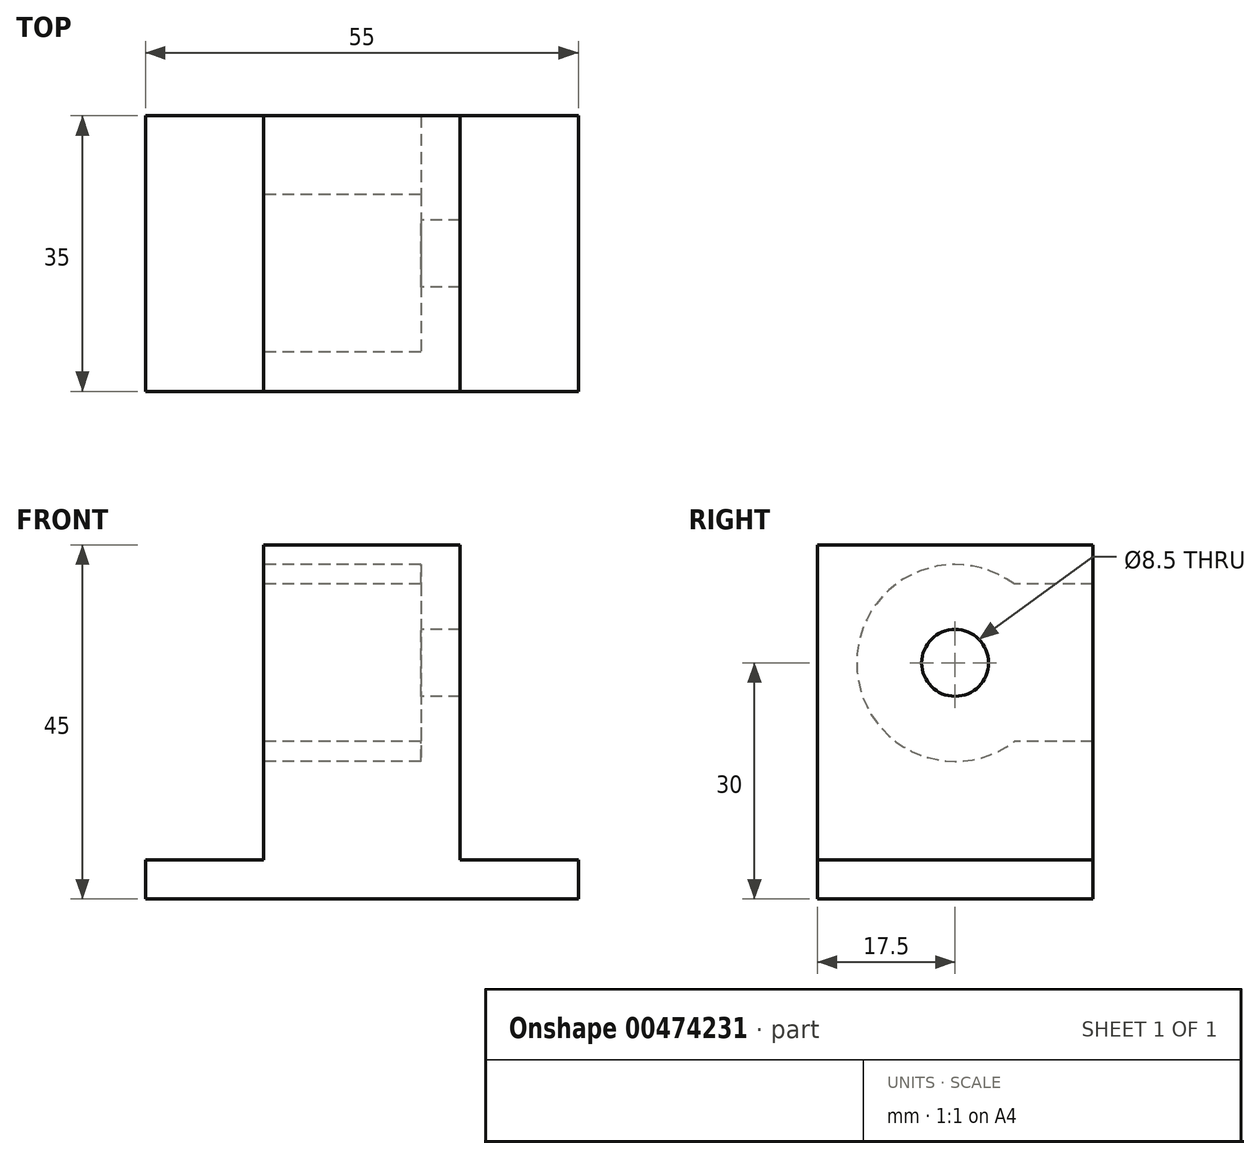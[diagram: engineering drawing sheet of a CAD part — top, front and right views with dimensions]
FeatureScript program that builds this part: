
annotation { "Feature Type Name" : "Feature", "Feature Type Description" : "" }
export const myFeature = defineFeature(function(context is Context, id is Id, definition is map)
    precondition{}
    {
        {
            var Q0;
            Q0=qCreatedBy(makeId("Top.planeOp"),FACE);
            var sketch = newSketch(context, id + "F0", { "sketchPlane" : qUnion([Q0])});
            skLineSegment(sketch, "E0.bottom", {"start": v(0, 0) * mm, "end": v(25, 0) * mm});
            skLineSegment(sketch, "E0.top", {"start": v(0, 35) * mm, "end": v(25, 35) * mm});
            skLineSegment(sketch, "E0.left", {"start": v(0, 0) * mm, "end": v(0, 35) * mm});
            skLineSegment(sketch, "E0.right", {"start": v(25, 0) * mm, "end": v(25, 35) * mm});
            skSolve(sketch);
        }
        {
            var Q0;
            Q0=makeQuery(id+"F0.imprint","IMPRINT",FACE,{"disambiguationData":[TD([[makeQuery(id+"F0.imprint","IMPRINT",EDGE,{"derivedFrom":sQuery(id+"F0.wireOp",EDGE,"E0.bottom")}),1.0]])]});
            extrude(context, id + "F1", {"entities" : qUnion([Q0]), "depth" : 45 * mm});
        }
        {
            var Q0;
            Q0=qCreatedBy(makeId("Right.planeOp"),FACE);
            var sketch = newSketch(context, id + "F2", { "sketchPlane" : qUnion([Q0])});
            skCircle(sketch, "E1", {"center": v(17.5, 30) * mm, "radius": 12.5 * mm});
            skSolve(sketch);
        }
        {
            var Q0;
            Q0=makeQuery(id+"F2.imprint","IMPRINT",FACE,{"disambiguationData":[TD([[makeQuery(id+"F2.imprint","IMPRINT",EDGE,{"derivedFrom":sQuery(id+"F2.wireOp",EDGE,"E1")}),1.0]])]});
            extrude(context, id + "F3", {"entities" : qUnion([Q0]), "operationType" : NewBodyOperationType.REMOVE, "depth" : 20 * mm});
        }
        {
            var Q0;
            Q0=qCreatedBy(makeId("Right.planeOp"),FACE);
            var sketch = newSketch(context, id + "F4", { "sketchPlane" : qUnion([Q0])});
            skCircle(sketch, "E2", {"center": v(17.5, 30) * mm, "radius": 4.25 * mm});
            skSolve(sketch);
        }
        {
            var Q0;
            Q0 = qSketchRegion(id + "F4", true);
            extrude(context, id + "F5", {"entities" : qUnion([Q0]), "operationType" : NewBodyOperationType.REMOVE, "depth" : 25 * mm});
        }
        {
            var Q0;
            Q0=qCreatedBy(makeId("Right.planeOp"),FACE);
            var sketch = newSketch(context, id + "F6", { "sketchPlane" : qUnion([Q0])});
            skLineSegment(sketch, "E3.bottom", {"start": v(0, 0) * mm, "end": v(35, 0) * mm});
            skLineSegment(sketch, "E3.top", {"start": v(0, 5) * mm, "end": v(35, 5) * mm});
            skLineSegment(sketch, "E3.left", {"start": v(0, 0) * mm, "end": v(0, 5) * mm});
            skLineSegment(sketch, "E3.right", {"start": v(35, 0) * mm, "end": v(35, 5) * mm});
            skSolve(sketch);
        }
        {
            var Q0;
            Q0 = qSketchRegion(id + "F6", true);
            extrude(context, id + "F7", {"entities" : qUnion([Q0]), "operationType" : NewBodyOperationType.ADD, "oppositeDirection" : true, "depth" : 15 * mm});
        }
        {
            var Q0;
            Q0=qCreatedBy(makeId("Right.planeOp"),FACE);
            var sketch = newSketch(context, id + "F8", { "sketchPlane" : qUnion([Q0])});
            skLineSegment(sketch, "E4.bottom", {"start": v(0, 0) * mm, "end": v(35, 0) * mm});
            skLineSegment(sketch, "E4.top", {"start": v(0, 5) * mm, "end": v(35, 5) * mm});
            skLineSegment(sketch, "E4.left", {"start": v(0, 0) * mm, "end": v(0, 5) * mm});
            skLineSegment(sketch, "E4.right", {"start": v(35, 0) * mm, "end": v(35, 5) * mm});
            skSolve(sketch);
        }
        {
            var Q0;
            Q0 = qSketchRegion(id + "F8", true);
            extrude(context, id + "F9", {"entities" : qUnion([Q0]), "operationType" : NewBodyOperationType.ADD, "depth" : 40 * mm});
        }
        {
            var Q0;
            Q0=qCreatedBy(makeId("Right.planeOp"),FACE);
            var sketch = newSketch(context, id + "F10", { "sketchPlane" : qUnion([Q0])});
            skLineSegment(sketch, "E5.bottom", {"start": v(35, 40) * mm, "end": v(17.5, 40) * mm});
            skLineSegment(sketch, "E5.top", {"start": v(35, 20) * mm, "end": v(17.5, 20) * mm});
            skLineSegment(sketch, "E5.left", {"start": v(35, 40) * mm, "end": v(35, 20) * mm});
            skLineSegment(sketch, "E5.right", {"start": v(17.5, 40) * mm, "end": v(17.5, 20) * mm});
            skSolve(sketch);
        }
        {
            var Q0;
            Q0 = qSketchRegion(id + "F10", true);
            extrude(context, id + "F11", {"entities" : qUnion([Q0]), "operationType" : NewBodyOperationType.REMOVE, "depth" : 20 * mm});
        }
    });
